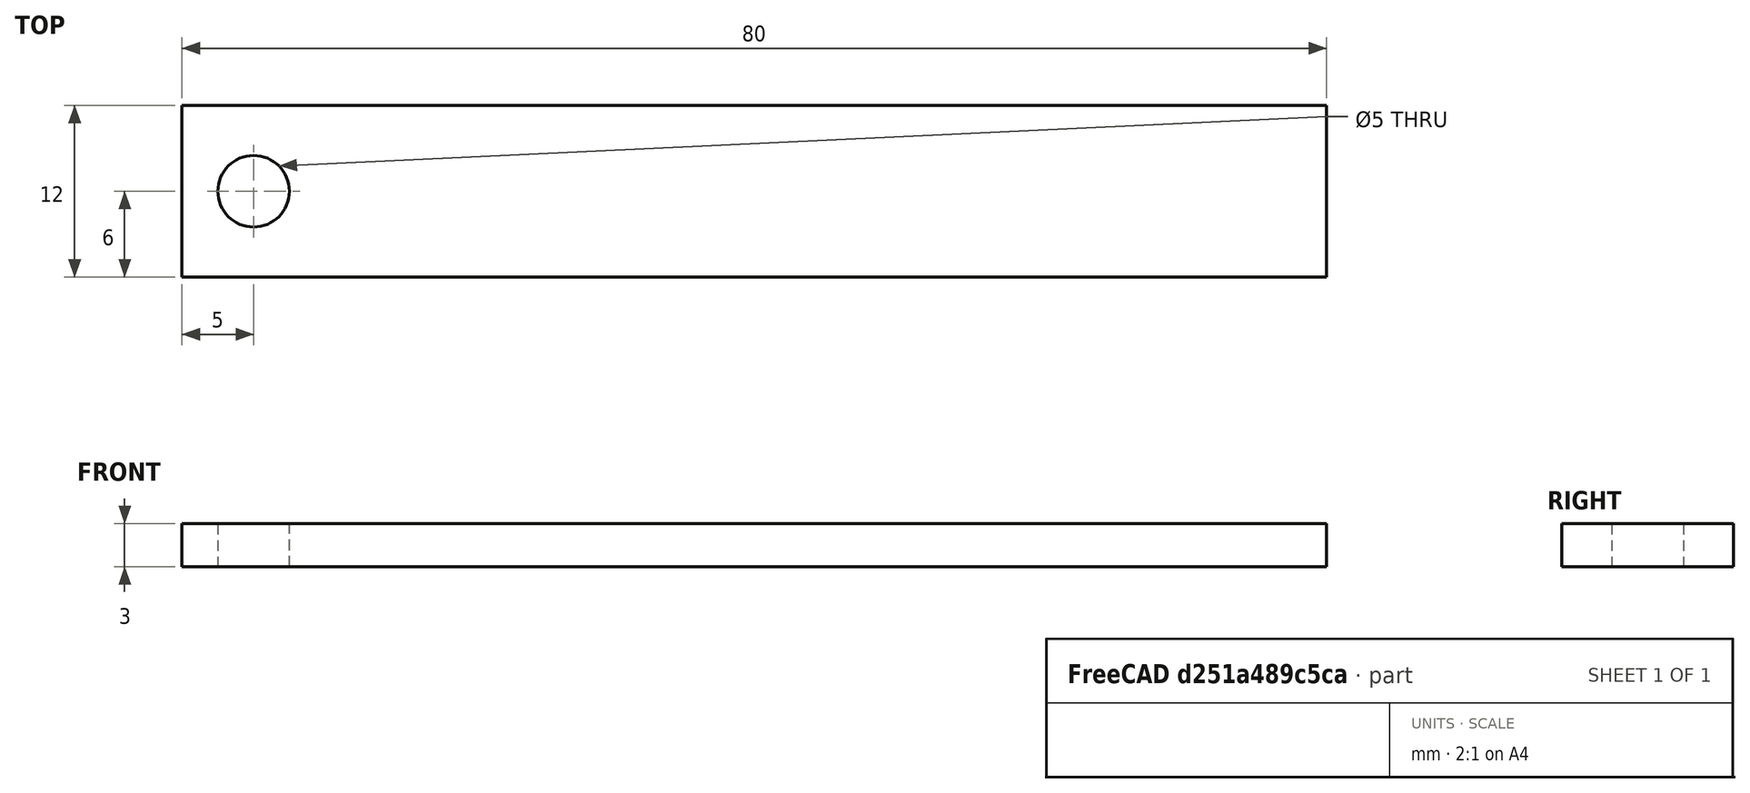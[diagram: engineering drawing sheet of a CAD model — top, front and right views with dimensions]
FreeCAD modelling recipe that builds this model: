
FCSTD DOCUMENT  (FreeCAD 0.21R33771 (Git))
Label: rectangle
License: All rights reserved
LicenseURL: http://en.wikipedia.org/wiki/All_rights_reserved
objects: Sketcher::SketchObject×1, Part::Extrusion×1, PartDesign::Line×1, App::Part×1
note: 3 computed .brp shape members not serialized (recipe doc carries the construction recipe); baked Part::Feature solids carry a one-line shape summary decoded from their .brp

FEATURE [Sketcher::SketchObject] Sketch
  FullyConstrained = true
  sketch-geometry (5):
    g0: LineSegment StartX=-40 StartY=6 StartZ=0 EndX=40 EndY=6 EndZ=0
    g1: LineSegment StartX=40 StartY=6 StartZ=0 EndX=40 EndY=-6 EndZ=0
    g2: LineSegment StartX=40 StartY=-6 StartZ=0 EndX=-40 EndY=-6 EndZ=0
    g3: LineSegment StartX=-40 StartY=-6 StartZ=0 EndX=-40 EndY=6 EndZ=0
    g4: Circle CenterX=-35 CenterY=0 CenterZ=0 NormalX=0 NormalY=0 NormalZ=1 AngleXU=0 Radius=2.5
  constraints (14):
    c: Coincident(g0,g1)
    c: Coincident(g1,g2)
    c: Coincident(g2,g3)
    c: Coincident(g3,g0)
    c: Horizontal(g0)
    c: Horizontal(g2)
    c: Vertical(g1)
    c: Vertical(g3)
    c: Symmetric(g2,g0,g-1)
    c: DistanceX(g0,g0) = 80
    c: DistanceY(g1,g1) = 12
    c: PointOnObject(g4,g-1)
    c: Diameter(g4) = 5
    c: DistanceX(g0,g4) = 5
FEATURE [Part::Extrusion] Extrude
  Base = -> Sketch
  Dir = (0,0,1)
  DirMode = 2
  FaceMakerClass = Part::FaceMakerBullseye
  LengthFwd = 3
  LengthRev = 0
  Solid = true
  Symmetric = false
FEATURE [PartDesign::Line] HoleAxis_1
  AttacherType = Attacher::AttachEngineLine
  Length = 7.04534
  MapMode = 19
  Placement = pos=(-35,0,3) rot=(0,0,1;0rad)
  ResizeMode = 1
  Support = -> [Extrude]
FEATURE [App::Part] Part  label="rectangle"
  Group = -> [Sketch,Extrude,HoleAxis_1]
  Origin = -> Origin
